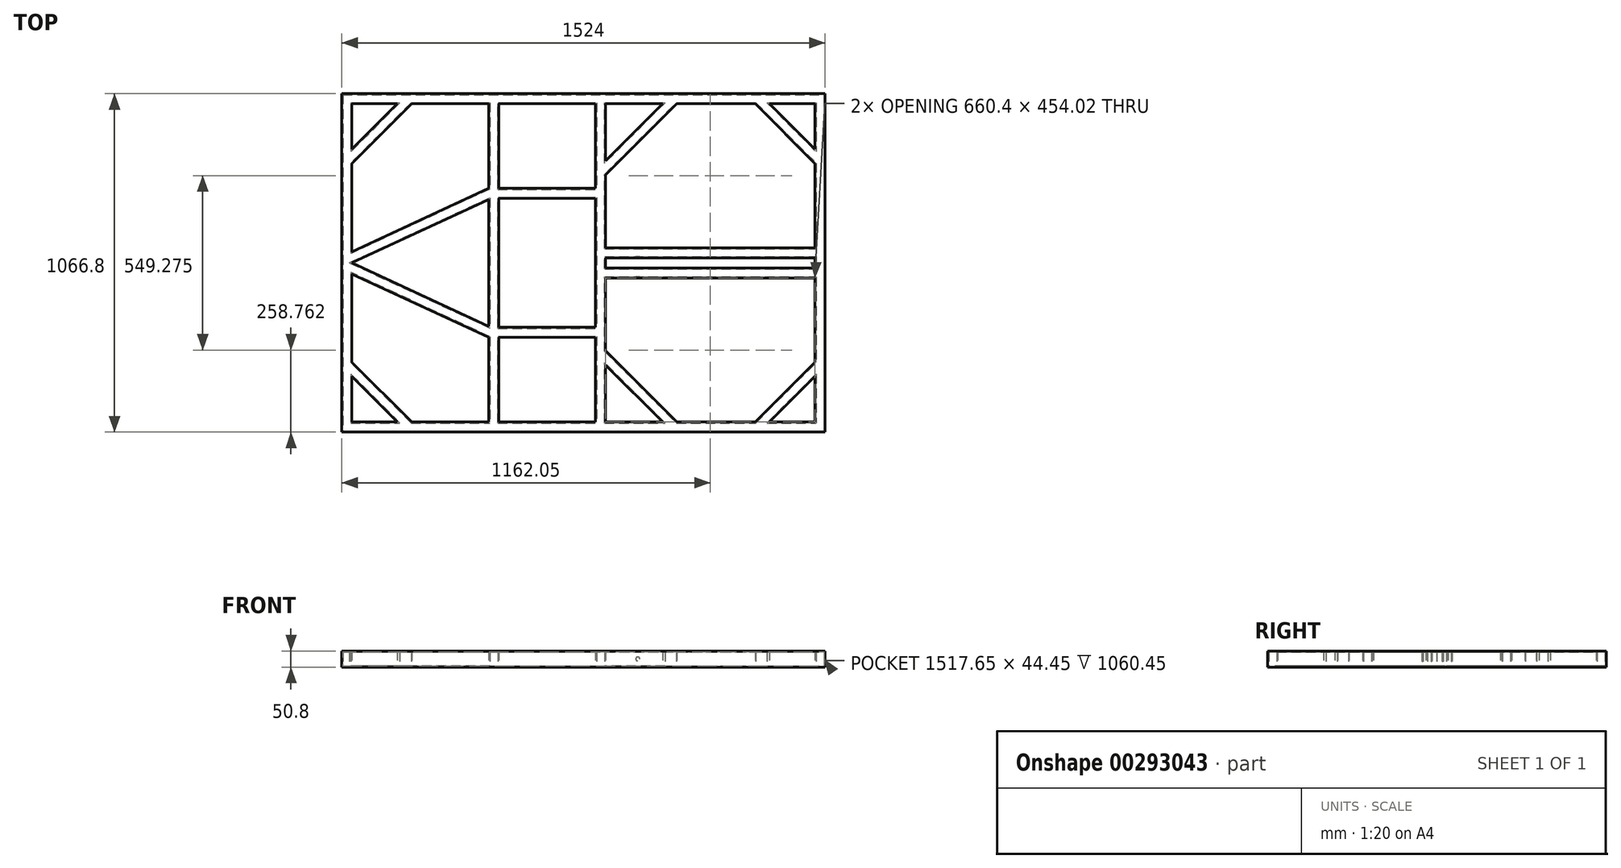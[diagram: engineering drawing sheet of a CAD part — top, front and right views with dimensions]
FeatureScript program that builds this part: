
annotation { "Feature Type Name" : "Feature", "Feature Type Description" : "" }
export const myFeature = defineFeature(function(context is Context, id is Id, definition is map)
    precondition{}
    {
        {
            var Q0;
            Q0=qCreatedBy(makeId("Top.planeOp"),FACE);
            var sketch = newSketch(context, id + "F0", { "sketchPlane" : qUnion([Q0])});
            skLineSegment(sketch, "E0.bottom", {"start": v(0, 0) * mm, "end": v(1524, 0) * mm});
            skLineSegment(sketch, "E0.top", {"start": v(0, -1066.8) * mm, "end": v(1524, -1066.8) * mm});
            skLineSegment(sketch, "E0.left", {"start": v(0, 0) * mm, "end": v(0, -1066.8) * mm});
            skLineSegment(sketch, "E0.right", {"start": v(1524, 0) * mm, "end": v(1524, -1066.8) * mm});
            skLineSegment(sketch, "E1.0", {"start": v(31.75, -31.75) * mm, "end": v(463.55, -31.75) * mm});
            skLineSegment(sketch, "E1.1", {"start": v(31.75, -31.75) * mm, "end": v(31.75, -1035.05) * mm});
            skLineSegment(sketch, "E1.2", {"start": v(31.75, -1035.05) * mm, "end": v(463.55, -1035.05) * mm});
            skLineSegment(sketch, "E1.3", {"start": v(1492.25, -31.75) * mm, "end": v(1492.25, -485.77) * mm});
            skLineSegment(sketch, "E2", {"start": v(463.55, -31.75) * mm, "end": v(463.55, -1035.05) * mm});
            skLineSegment(sketch, "E3", {"start": v(495.3, -1035.05) * mm, "end": v(495.3, -31.75) * mm});
            skLineSegment(sketch, "E4", {"start": v(800.1, -31.75) * mm, "end": v(800.1, -1035.05) * mm});
            skLineSegment(sketch, "E5", {"start": v(831.85, -1035.05) * mm, "end": v(831.85, -581.02) * mm});
            skLineSegment(sketch, "E6.trimOffspring", {"start": v(831.85, -1035.05) * mm, "end": v(1492.25, -1035.05) * mm});
            skLineSegment(sketch, "E7.trimOffspring", {"start": v(495.3, -1035.05) * mm, "end": v(800.1, -1035.05) * mm});
            skLineSegment(sketch, "E8.trimOffspring", {"start": v(495.3, -31.75) * mm, "end": v(800.1, -31.75) * mm});
            skLineSegment(sketch, "E9.trimOffspring", {"start": v(831.85, -31.75) * mm, "end": v(1492.25, -31.75) * mm});
            skLineSegment(sketch, "E10", {"start": v(31.75, -533.4) * mm, "end": v(2205.19, -533.4) * mm, "construction": true});
            skLineSegment(sketch, "E11.bottom", {"start": v(831.85, -517.52) * mm, "end": v(1492.25, -517.52) * mm});
            skLineSegment(sketch, "E11.top", {"start": v(831.85, -485.77) * mm, "end": v(1492.25, -485.77) * mm});
            skLineSegment(sketch, "E12.trimOffspring", {"start": v(831.85, -485.77) * mm, "end": v(831.85, -31.75) * mm});
            skLineSegment(sketch, "E13.trimOffspring", {"start": v(1492.25, -517.52) * mm, "end": v(1492.25, -549.27) * mm});
            skLineSegment(sketch, "E14.MirrorCS", {"start": v(831.85, -549.27) * mm, "end": v(1492.25, -549.27) * mm});
            skLineSegment(sketch, "E15.MirrorCS", {"start": v(831.85, -581.02) * mm, "end": v(1492.25, -581.02) * mm});
            skLineSegment(sketch, "E16.trimOffspring", {"start": v(831.85, -549.27) * mm, "end": v(831.85, -517.52) * mm});
            skLineSegment(sketch, "E17.trimOffspring", {"start": v(1492.25, -581.02) * mm, "end": v(1492.25, -1035.05) * mm});
            skLineSegment(sketch, "E18.left", {"start": v(31.75, -788.03) * mm, "end": v(31.75, -832.48) * mm});
            skLineSegment(sketch, "E19.right", {"start": v(1492.25, -788.03) * mm, "end": v(1492.25, -832.48) * mm});
            skLineSegment(sketch, "E20.bottom", {"start": v(495.3, -736.6) * mm, "end": v(800.1, -736.6) * mm});
            skLineSegment(sketch, "E20.top", {"start": v(495.3, -768.35) * mm, "end": v(800.1, -768.35) * mm});
            skLineSegment(sketch, "E20.left", {"start": v(495.3, -736.6) * mm, "end": v(495.3, -768.35) * mm});
            skLineSegment(sketch, "E20.right", {"start": v(800.1, -736.6) * mm, "end": v(800.1, -768.35) * mm});
            skLineSegment(sketch, "E21", {"start": v(175.43, -31.75) * mm, "end": v(31.75, -175.43) * mm});
            skLineSegment(sketch, "E22", {"start": v(220.34, -31.75) * mm, "end": v(31.75, -220.34) * mm});
            skLineSegment(sketch, "E23", {"start": v(762, -1066.8) * mm, "end": v(762, 0) * mm, "construction": true});
            skLineSegment(sketch, "E24.MirrorCS", {"start": v(1348.57, -31.75) * mm, "end": v(1492.25, -175.43) * mm});
            skLineSegment(sketch, "E25.MirrorCS", {"start": v(1303.66, -31.75) * mm, "end": v(1492.25, -220.34) * mm});
            skLineSegment(sketch, "E26.MirrorCS", {"start": v(220.34, -1035.05) * mm, "end": v(31.75, -846.46) * mm});
            skLineSegment(sketch, "E27.MirrorCS", {"start": v(175.43, -1035.05) * mm, "end": v(31.75, -891.37) * mm});
            skLineSegment(sketch, "E28.MirrorCS", {"start": v(1303.66, -1035.05) * mm, "end": v(1492.25, -846.46) * mm});
            skLineSegment(sketch, "E29.MirrorCS", {"start": v(1348.57, -1035.05) * mm, "end": v(1492.25, -891.37) * mm});
            skLineSegment(sketch, "E30.MirrorCS", {"start": v(495.3, -330.2) * mm, "end": v(800.1, -330.2) * mm});
            skLineSegment(sketch, "E31.MirrorCS", {"start": v(495.3, -298.45) * mm, "end": v(800.1, -298.45) * mm});
            skLineSegment(sketch, "E32", {"start": v(463.55, -298.45) * mm, "end": v(31.75, -498.41) * mm});
            skLineSegment(sketch, "E33", {"start": v(31.75, -533.4) * mm, "end": v(463.55, -333.44) * mm});
            skLineSegment(sketch, "E34.MirrorCS", {"start": v(31.75, -533.4) * mm, "end": v(463.55, -733.36) * mm});
            skLineSegment(sketch, "E35.MirrorCS", {"start": v(463.55, -768.35) * mm, "end": v(31.75, -568.39) * mm});
            skLineSegment(sketch, "E36", {"start": v(1011.46, -31.75) * mm, "end": v(831.85, -211.36) * mm});
            skLineSegment(sketch, "E37", {"start": v(831.85, -256.26) * mm, "end": v(1056.36, -31.75) * mm});
            skLineSegment(sketch, "E38.MirrorCS", {"start": v(831.85, -810.54) * mm, "end": v(1056.36, -1035.05) * mm});
            skLineSegment(sketch, "E39.MirrorCS", {"start": v(1011.46, -1035.05) * mm, "end": v(831.85, -855.44) * mm});
            skSolve(sketch);
        }
        {
            var Q0;
            {var subQ0=sQuery(id+"F0.wireOp",EDGE,"E21");Q0=makeQuery(id+"F0.imprint","IMPRINT",FACE,{"disambiguationData":[TD([[makeQuery(id+"F0.imprint","IMPRINT",EDGE,{"derivedFrom":subQ0}),1.0]])]});}
            var Q1;
            Q1=makeQuery(id+"F0.imprint","IMPRINT",FACE,{"disambiguationData":[TD([[makeQuery(id+"F0.imprint","IMPRINT",EDGE,{"derivedFrom":sQuery(id+"F0.wireOp",EDGE,"E0.bottom")}),-1.0]])]});
            var Q2;
            {var subQ0=sQuery(id+"F0.wireOp",EDGE,"E26.MirrorCS");Q2=makeQuery(id+"F0.imprint","IMPRINT",FACE,{"disambiguationData":[TD([[makeQuery(id+"F0.imprint","IMPRINT",EDGE,{"derivedFrom":subQ0}),1.0]])]});}
            var Q3;
            Q3=makeQuery(id+"F0.imprint","IMPRINT",FACE,{"disambiguationData":[TD([[makeQuery(id+"F0.imprint","IMPRINT",EDGE,{"derivedFrom":sQuery(id+"F0.wireOp",EDGE,"E20.bottom")}),-1.0]])]});
            var Q4;
            {var subQ0=sQuery(id+"F0.wireOp",EDGE,"E28.MirrorCS");Q4=makeQuery(id+"F0.imprint","IMPRINT",FACE,{"disambiguationData":[TD([[makeQuery(id+"F0.imprint","IMPRINT",EDGE,{"derivedFrom":subQ0}),-1.0]])]});}
            var Q5;
            {var subQ0=sQuery(id+"F0.wireOp",EDGE,"E24.MirrorCS");Q5=makeQuery(id+"F0.imprint","IMPRINT",FACE,{"disambiguationData":[TD([[makeQuery(id+"F0.imprint","IMPRINT",EDGE,{"derivedFrom":subQ0}),-1.0]])]});}
            var Q6;
            {var subQ0=sQuery(id+"F0.wireOp",EDGE,"E30.MirrorCS");Q6=makeQuery(id+"F0.imprint","IMPRINT",FACE,{"disambiguationData":[TD([[makeQuery(id+"F0.imprint","IMPRINT",EDGE,{"derivedFrom":subQ0}),1.0]])]});}
            var Q7;
            {var subQ0=sQuery(id+"F0.wireOp",EDGE,"E32");Q7=makeQuery(id+"F0.imprint","IMPRINT",FACE,{"disambiguationData":[TD([[makeQuery(id+"F0.imprint","IMPRINT",EDGE,{"derivedFrom":subQ0}),1.0]])]});}
            var Q8;
            {var subQ0=sQuery(id+"F0.wireOp",EDGE,"E34.MirrorCS");Q8=makeQuery(id+"F0.imprint","IMPRINT",FACE,{"disambiguationData":[TD([[makeQuery(id+"F0.imprint","IMPRINT",EDGE,{"derivedFrom":subQ0}),-1.0]])]});}
            var Q9;
            {var subQ0=sQuery(id+"F0.wireOp",EDGE,"E36");Q9=makeQuery(id+"F0.imprint","IMPRINT",FACE,{"disambiguationData":[TD([[makeQuery(id+"F0.imprint","IMPRINT",EDGE,{"derivedFrom":subQ0}),1.0]])]});}
            var Q10;
            {var subQ0=sQuery(id+"F0.wireOp",EDGE,"E38.MirrorCS");Q10=makeQuery(id+"F0.imprint","IMPRINT",FACE,{"disambiguationData":[TD([[makeQuery(id+"F0.imprint","IMPRINT",EDGE,{"derivedFrom":subQ0}),-1.0]])]});}
            extrude(context, id + "F1", {"entities" : qUnion([Q0, Q1, Q2, Q3, Q4, Q5, Q6, Q7, Q8, Q9, Q10]), "depth" : 50.8 * mm});
        }
        {
            var Q0;
            Q0=makeQuery(id+"F1.opExtrude","SWEPT_FACE",FACE,{"disambiguationData":[OSD([sQuery(id+"F0.wireOp",EDGE,"E2")])]});
            var sketch = newSketch(context, id + "F2", { "sketchPlane" : qUnion([Q0])});
            skLineSegment(sketch, "E40", {"start": v(31.75, 25.4) * mm, "end": v(1035.05, 25.4) * mm, "construction": true});
            skCircle(sketch, "E41", {"center": v(381, 25.4) * mm, "radius": 12.7 * mm});
            skPoint(sketch, "E42", {"position": v(533.4, 25.4) * mm});
            skLineSegment(sketch, "E43", {"start": v(533.4, 25.4) * mm, "end": v(533.4, 0) * mm, "construction": true});
            skCircle(sketch, "E44.MirrorC", {"center": v(685.8, 25.4) * mm, "radius": 12.7 * mm});
            skSolve(sketch);
        }
        {
            var Q0;
            Q0=makeQuery(id+"F1.opExtrude","SWEPT_FACE",FACE,{"disambiguationData":[OSD([sQuery(id+"F0.wireOp",EDGE,"E11.top")])]});
            var sketch = newSketch(context, id + "F3", { "sketchPlane" : qUnion([Q0])});
            skLineSegment(sketch, "E45.0.0", {"start": v(-1492.25, 0) * mm, "end": v(-831.85, 0) * mm});
            skLineSegment(sketch, "E45.0.1", {"start": v(-831.85, 0) * mm, "end": v(-831.85, 50.8) * mm});
            skLineSegment(sketch, "E45.0.2", {"start": v(-831.85, 50.8) * mm, "end": v(-1492.25, 50.8) * mm});
            skLineSegment(sketch, "E45.0.3", {"start": v(-1492.25, 50.8) * mm, "end": v(-1492.25, 0) * mm});
            skCircle(sketch, "E46", {"center": v(-933.45, 25.4) * mm, "radius": 6.35 * mm});
            skPoint(sketch, "E46.centerSnap0", {"position": v(-831.85, 25.4) * mm});
            skSolve(sketch);
        }
        {
            var Q0;
            Q0=makeQuery(id+"F3.imprint","IMPRINT",FACE,{"disambiguationData":[TD([[makeQuery(id+"F3.imprint","IMPRINT",EDGE,{"derivedFrom":sQuery(id+"F3.wireOp",EDGE,"E46")}),1.0]])]});
            extrude(context, id + "F4", {"entities" : qUnion([Q0]), "operationType" : NewBodyOperationType.REMOVE, "oppositeDirection" : true, "depth" : 127 * mm});
        }
        {
            var Q0;
            Q0=makeQuery(id+"FJD3ntM57F8SJmY_1.boolean.opBoolean","COPY",FACE,{"disambiguationData":[TD([makeQuery(id+"F1.opExtrude","SWEPT_FACE",FACE,{"disambiguationData":[OSD([sQuery(id+"F0.wireOp",EDGE,"E4")])]})])],"derivedFrom":makeQuery(id+"FJD3ntM57F8SJmY_1.opExtrude","SWEPT_FACE",FACE,{"disambiguationData":[OSD([sQuery(id+"F2.wireOp",EDGE,"E41")])]})});
            var Q1;
            Q1=makeQuery(id+"FJD3ntM57F8SJmY_1.boolean.opBoolean","COPY",FACE,{"disambiguationData":[TD([makeQuery(id+"F1.opExtrude","SWEPT_FACE",FACE,{"disambiguationData":[OSD([sQuery(id+"F0.wireOp",EDGE,"E4")])]})])],"derivedFrom":makeQuery(id+"FJD3ntM57F8SJmY_1.opExtrude","SWEPT_FACE",FACE,{"disambiguationData":[OSD([sQuery(id+"F2.wireOp",EDGE,"f3b9bb93-9202-470c-8418-00dd5162cf0f0.MirrorC")])]})});
            var Q2;
            Q2=makeQuery(id+"FJD3ntM57F8SJmY_1.boolean.opBoolean","COPY",FACE,{"disambiguationData":[TD([makeQuery(id+"F1.opExtrude","SWEPT_FACE",FACE,{"disambiguationData":[OSD([sQuery(id+"F0.wireOp",EDGE,"E2")])]})])],"derivedFrom":makeQuery(id+"FJD3ntM57F8SJmY_1.opExtrude","SWEPT_FACE",FACE,{"disambiguationData":[OSD([sQuery(id+"F2.wireOp",EDGE,"E41")])]})});
            var Q3;
            Q3=makeQuery(id+"FJD3ntM57F8SJmY_1.boolean.opBoolean","COPY",FACE,{"disambiguationData":[TD([makeQuery(id+"F1.opExtrude","SWEPT_FACE",FACE,{"disambiguationData":[OSD([sQuery(id+"F0.wireOp",EDGE,"E2")])]})])],"derivedFrom":makeQuery(id+"FJD3ntM57F8SJmY_1.opExtrude","SWEPT_FACE",FACE,{"disambiguationData":[OSD([sQuery(id+"F2.wireOp",EDGE,"f3b9bb93-9202-470c-8418-00dd5162cf0f0.MirrorC")])]})});
            var Q4;
            Q4=makeQuery(id+"F4.boolean.opBoolean","COPY",FACE,{"disambiguationData":[TD([makeQuery(id+"F1.opExtrude","SWEPT_FACE",FACE,{"disambiguationData":[OSD([sQuery(id+"F0.wireOp",EDGE,"E14.MirrorCS")])]})])],"derivedFrom":makeQuery(id+"F4.opExtrude","SWEPT_FACE",FACE,{"disambiguationData":[OSD([sQuery(id+"F3.wireOp",EDGE,"E46")])]})});
            var Q5;
            Q5=makeQuery(id+"F4.boolean.opBoolean","COPY",FACE,{"disambiguationData":[TD([makeQuery(id+"F1.opExtrude","SWEPT_FACE",FACE,{"disambiguationData":[OSD([sQuery(id+"F0.wireOp",EDGE,"E11.bottom")])]})])],"derivedFrom":makeQuery(id+"F4.opExtrude","SWEPT_FACE",FACE,{"disambiguationData":[OSD([sQuery(id+"F3.wireOp",EDGE,"E46")])]})});
            shell(context, id + "F5", {"entities" : qUnion([Q0, Q1, Q2, Q3, Q4, Q5]), "thickness" : 3.17 * mm});
        }
    });
